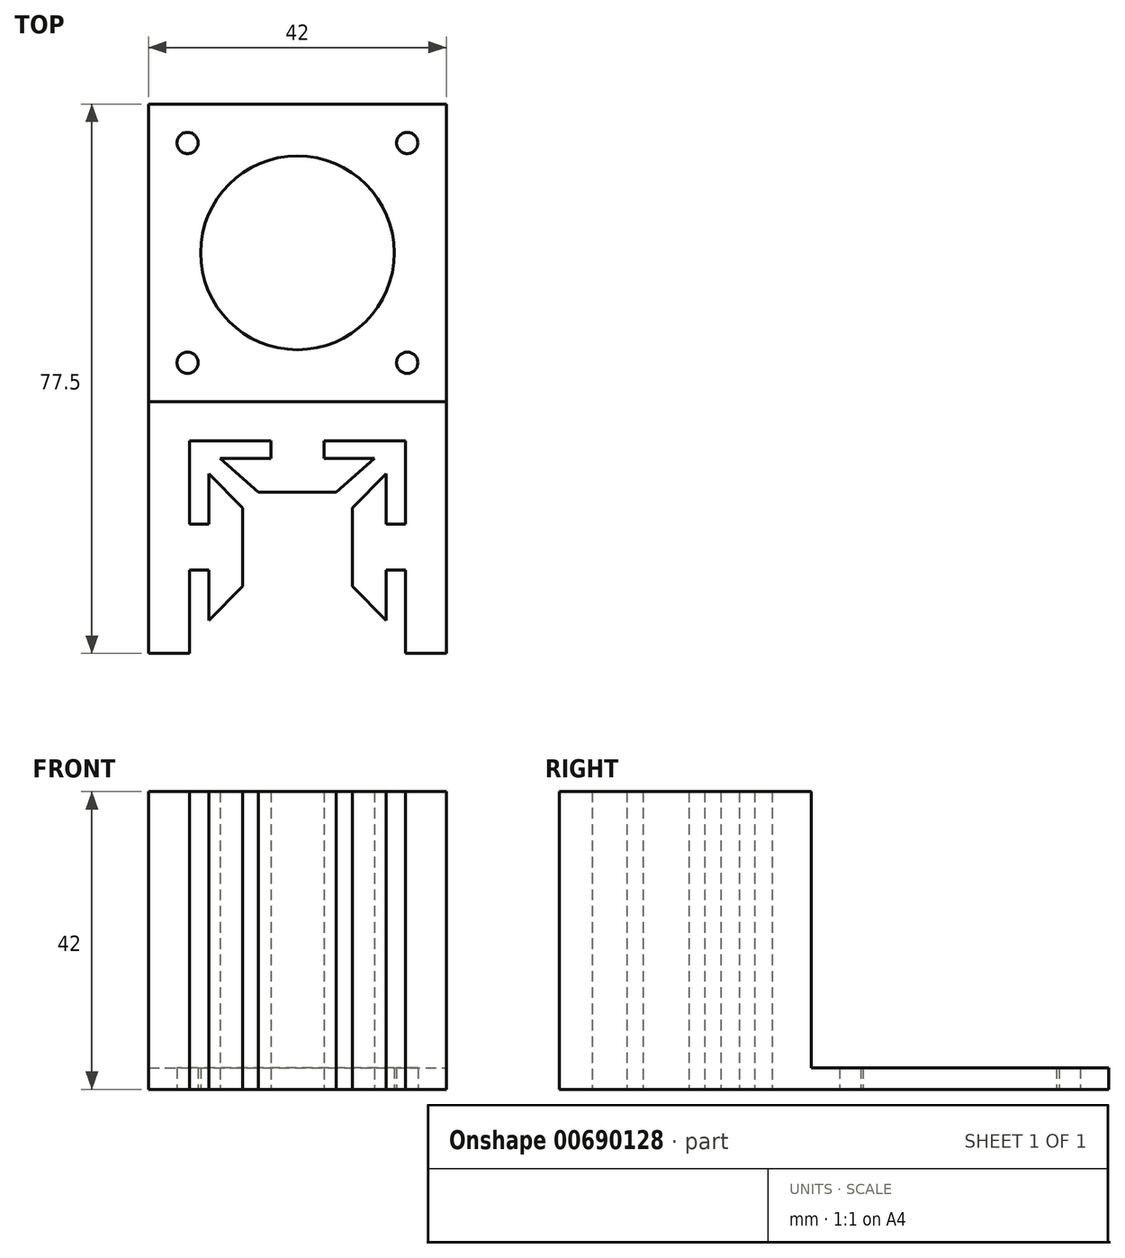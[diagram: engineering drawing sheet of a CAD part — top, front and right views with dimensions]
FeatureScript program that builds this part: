
annotation { "Feature Type Name" : "Feature", "Feature Type Description" : "" }
export const myFeature = defineFeature(function(context is Context, id is Id, definition is map)
    precondition{}
    {
        {
            var Q0;
            Q0=qCreatedBy(makeId("Top.planeOp"),FACE);
            var sketch = newSketch(context, id + "F0", { "sketchPlane" : qUnion([Q0])});
            skPoint(sketch, "E0.middle", {"position": v(0, 0) * mm});
            skLineSegment(sketch, "E1.bottom", {"start": v(-21, 21) * mm, "end": v(21, 21) * mm});
            skLineSegment(sketch, "E1.top", {"start": v(-21, -21) * mm, "end": v(21, -21) * mm});
            skLineSegment(sketch, "E1.left", {"start": v(-21, 21) * mm, "end": v(-21, -21) * mm});
            skLineSegment(sketch, "E1.right", {"start": v(21, 21) * mm, "end": v(21, -21) * mm});
            skLineSegment(sketch, "E2.bottom", {"start": v(15.5, -15.5) * mm, "end": v(-15.5, -15.5) * mm, "construction": true});
            skLineSegment(sketch, "E2.top", {"start": v(15.5, 15.5) * mm, "end": v(-15.5, 15.5) * mm, "construction": true});
            skLineSegment(sketch, "E2.left", {"start": v(15.5, -15.5) * mm, "end": v(15.5, 15.5) * mm, "construction": true});
            skLineSegment(sketch, "E2.right", {"start": v(-15.5, -15.5) * mm, "end": v(-15.5, 15.5) * mm, "construction": true});
            skCircle(sketch, "E3", {"center": v(-15.5, 15.5) * mm, "radius": 1.5 * mm});
            skCircle(sketch, "E4", {"center": v(15.5, 15.5) * mm, "radius": 1.5 * mm});
            skCircle(sketch, "E5", {"center": v(-15.5, -15.5) * mm, "radius": 1.5 * mm});
            skCircle(sketch, "E6", {"center": v(15.5, -15.5) * mm, "radius": 1.5 * mm});
            skLineSegment(sketch, "E7", {"start": v(0, -21) * mm, "end": v(3.25, -21) * mm});
            skLineSegment(sketch, "E8.MirrorCS", {"start": v(0, -21) * mm, "end": v(-3.25, -21) * mm});
            skLineSegment(sketch, "E9.left", {"start": v(-21, -21) * mm, "end": v(-21, -26.5) * mm});
            skLineSegment(sketch, "E9.right", {"start": v(21, -21) * mm, "end": v(21, -26.5) * mm});
            skCircle(sketch, "E10", {"center": v(0, 0) * mm, "radius": 13.67 * mm});
            skLineSegment(sketch, "E11", {"start": v(0, -26.5) * mm, "end": v(0, -33.75) * mm, "construction": true});
            skLineSegment(sketch, "E12", {"start": v(-3.75, -26.5) * mm, "end": v(-3.75, -29) * mm});
            skLineSegment(sketch, "E13", {"start": v(-3.75, -29) * mm, "end": v(-10.88, -29) * mm});
            skLineSegment(sketch, "E14", {"start": v(0, -33.75) * mm, "end": v(-5.5, -33.75) * mm});
            skLineSegment(sketch, "E15", {"start": v(-5.5, -33.75) * mm, "end": v(-10.88, -29) * mm});
            skLineSegment(sketch, "E16.MirrorCS", {"start": v(5.5, -33.75) * mm, "end": v(10.88, -29) * mm});
            skLineSegment(sketch, "E17.MirrorCS", {"start": v(3.75, -29) * mm, "end": v(10.88, -29) * mm});
            skLineSegment(sketch, "E18.MirrorCS", {"start": v(3.75, -26.5) * mm, "end": v(3.75, -29) * mm});
            skLineSegment(sketch, "E19.MirrorCS", {"start": v(0, -33.75) * mm, "end": v(5.5, -33.75) * mm});
            skLineSegment(sketch, "E20", {"start": v(0, -26.5) * mm, "end": v(-15.25, -26.5) * mm});
            skLineSegment(sketch, "E21", {"start": v(-15, -41.5) * mm, "end": v(-7.75, -41.5) * mm, "construction": true});
            skLineSegment(sketch, "E22", {"start": v(-7.75, -41.5) * mm, "end": v(-7.75, -36) * mm});
            skLineSegment(sketch, "E23", {"start": v(-12.5, -38.25) * mm, "end": v(-12.5, -31.12) * mm});
            skLineSegment(sketch, "E24", {"start": v(-12.5, -31.12) * mm, "end": v(-7.75, -36) * mm});
            skLineSegment(sketch, "E25.MirrorCS", {"start": v(-7.75, -41.5) * mm, "end": v(-7.75, -47) * mm});
            skLineSegment(sketch, "E26.MirrorCS", {"start": v(-12.5, -51.88) * mm, "end": v(-7.75, -47) * mm});
            skLineSegment(sketch, "E27.MirrorCS", {"start": v(-12.5, -44.75) * mm, "end": v(-12.5, -51.88) * mm});
            skLineSegment(sketch, "E28.MirrorCS", {"start": v(7.75, -41.5) * mm, "end": v(7.75, -47) * mm});
            skLineSegment(sketch, "E29.MirrorCS", {"start": v(7.75, -41.5) * mm, "end": v(7.75, -36) * mm});
            skLineSegment(sketch, "E30.MirrorCS", {"start": v(12.5, -31.12) * mm, "end": v(7.75, -36) * mm});
            skLineSegment(sketch, "E31.MirrorCS", {"start": v(12.5, -38.25) * mm, "end": v(12.5, -31.12) * mm});
            skLineSegment(sketch, "E32.MirrorCS", {"start": v(12.5, -44.75) * mm, "end": v(12.5, -51.88) * mm});
            skLineSegment(sketch, "E33.MirrorCS", {"start": v(12.5, -51.88) * mm, "end": v(7.75, -47) * mm});
            skLineSegment(sketch, "E34", {"start": v(-15.25, -56.5) * mm, "end": v(-21, -56.5) * mm});
            skLineSegment(sketch, "E35", {"start": v(-21, -56.5) * mm, "end": v(-21, -26.5) * mm});
            skLineSegment(sketch, "E36", {"start": v(15.25, -56.5) * mm, "end": v(21, -56.5) * mm});
            skLineSegment(sketch, "E37", {"start": v(21, -56.5) * mm, "end": v(21, -26.5) * mm});
            skLineSegment(sketch, "E38", {"start": v(-15.25, -26.5) * mm, "end": v(-15.25, -56.5) * mm});
            skLineSegment(sketch, "E39", {"start": v(-12.5, -38.25) * mm, "end": v(-15.25, -38.25) * mm});
            skLineSegment(sketch, "E40", {"start": v(-12.5, -44.75) * mm, "end": v(-15.25, -44.75) * mm});
            skLineSegment(sketch, "E41.MirrorCS", {"start": v(12.5, -44.75) * mm, "end": v(15.25, -44.75) * mm});
            skLineSegment(sketch, "E42.MirrorCS", {"start": v(12.5, -38.25) * mm, "end": v(15.25, -38.25) * mm});
            skLineSegment(sketch, "E43.MirrorCS", {"start": v(0, -26.5) * mm, "end": v(15.25, -26.5) * mm});
            skLineSegment(sketch, "E44.MirrorCS", {"start": v(15.25, -26.5) * mm, "end": v(15.25, -56.5) * mm});
            skSolve(sketch);
        }
        {
            var Q0;
            Q0=makeQuery(id+"F0.imprint","IMPRINT",FACE,{"disambiguationData":[TD([[makeQuery(id+"F0.imprint","IMPRINT",EDGE,{"derivedFrom":sQuery(id+"F0.wireOp",EDGE,"E1.bottom")}),-1.0]])]});
            extrude(context, id + "F1", {"entities" : qUnion([Q0]), "depth" : 3 * mm, "offsetDistance" : 25 * mm});
        }
        {
            var Q0;
            Q0=makeQuery(id+"F0.imprint","IMPRINT",FACE,{"disambiguationData":[TD([[makeQuery(id+"F0.imprint","IMPRINT",EDGE,{"derivedFrom":sQuery(id+"F0.wireOp",EDGE,"E30.MirrorCS")}),1.0]])]});
            var Q1;
            {var subQ4=sQuery(id+"F0.wireOp",EDGE,"E36");Q1=makeQuery(id+"F0.imprint","IMPRINT",FACE,{"disambiguationData":[TD([[makeQuery(id+"F0.imprint","IMPRINT",EDGE,{"derivedFrom":subQ4}),1.0]])]});}
            var Q2;
            {var subQ3=sQuery(id+"F0.wireOp",EDGE,"E12");Q2=makeQuery(id+"F0.imprint","IMPRINT",FACE,{"disambiguationData":[TD([[makeQuery(id+"F0.imprint","IMPRINT",EDGE,{"derivedFrom":subQ3}),1.0]])]});}
            var Q3;
            Q3=makeQuery(id+"F0.imprint","IMPRINT",FACE,{"disambiguationData":[TD([[makeQuery(id+"F0.imprint","IMPRINT",EDGE,{"derivedFrom":sQuery(id+"F0.wireOp",EDGE,"E22")}),1.0]])]});
            var Q4;
            {var subQ3=sQuery(id+"F0.wireOp",EDGE,"xgqm9zbJ-35YR-MA57-3RnW-XfJJkj89ymEh");Q4=makeQuery(id+"F0.imprint","IMPRINT",FACE,{"disambiguationData":[TD([[makeQuery(id+"F0.imprint","IMPRINT",EDGE,{"derivedFrom":subQ3}),-1.0]])]});}
            var Q5;
            {var subQ6=sQuery(id+"F0.wireOp",EDGE,"E9.left");Q5=makeQuery(id+"F0.imprint","IMPRINT",FACE,{"disambiguationData":[TD([[makeQuery(id+"F0.imprint","IMPRINT",EDGE,{"derivedFrom":subQ6}),1.0]])]});}
            extrude(context, id + "F2", {"entities" : qUnion([Q0, Q1, Q2, Q3, Q4, Q5]), "operationType" : NewBodyOperationType.ADD, "depth" : 42 * mm, "offsetDistance" : 25 * mm});
        }
    });
